# Revit family: Ферма стропильная 24 м_10%
name_source: partatom
category: Каркас несущий
units: mm (PartAtom-declared; Revit-internal decimal feet)

## family parameters
Всегда вертикально = Да
Всегда экспортировать в виде геометрии = Нет
Заголовок OmniClass = Trussed Beams and Joists
Материал для поведения модели = Сталь
На основе рабочей плоскости = Нет
Номер OmniClass = 23.25.30.21.14
Общий = Нет
Показывать семейство разрезанным на планах = Да
При загрузке вырезать с полостями = Нет
Условное обозначение = Из семейства
Форма сечения = Не задано

## types (3) — shared parameters
ADSK_Группа конструкций = 4
ADSK_Тип элемента КМ = 1
Ферма стропильная ФС-24-10-2.86 = Нет

## per-type parameters (varying)
| type | ADSK_Марка | ADSK_Марка конструкции | ADSK_Масса | Ферма стропильная ФС-24-10-1.95 | Ферма стропильная ФС-24-10-2.4 |
| Ферма стропильная ФС-24-10-2.4 | ФC-24/10-2.40 | ФC-24/10-2.40 | 1920 | Нет | Да |
| Ферма стропильная ФС-24-10-1.95 | ФС-24-10-1.95 | ФС-24-10-1.95 | 1635 | Да | Нет |
| Ферма стропильная ФС-24-10-2.86 | ФС-24-10-2.86 | ФС-24-10-2.86 | 2201 | Да | Нет |

note: column(s) folded — value = type name in every type: ADSK_Наименование
